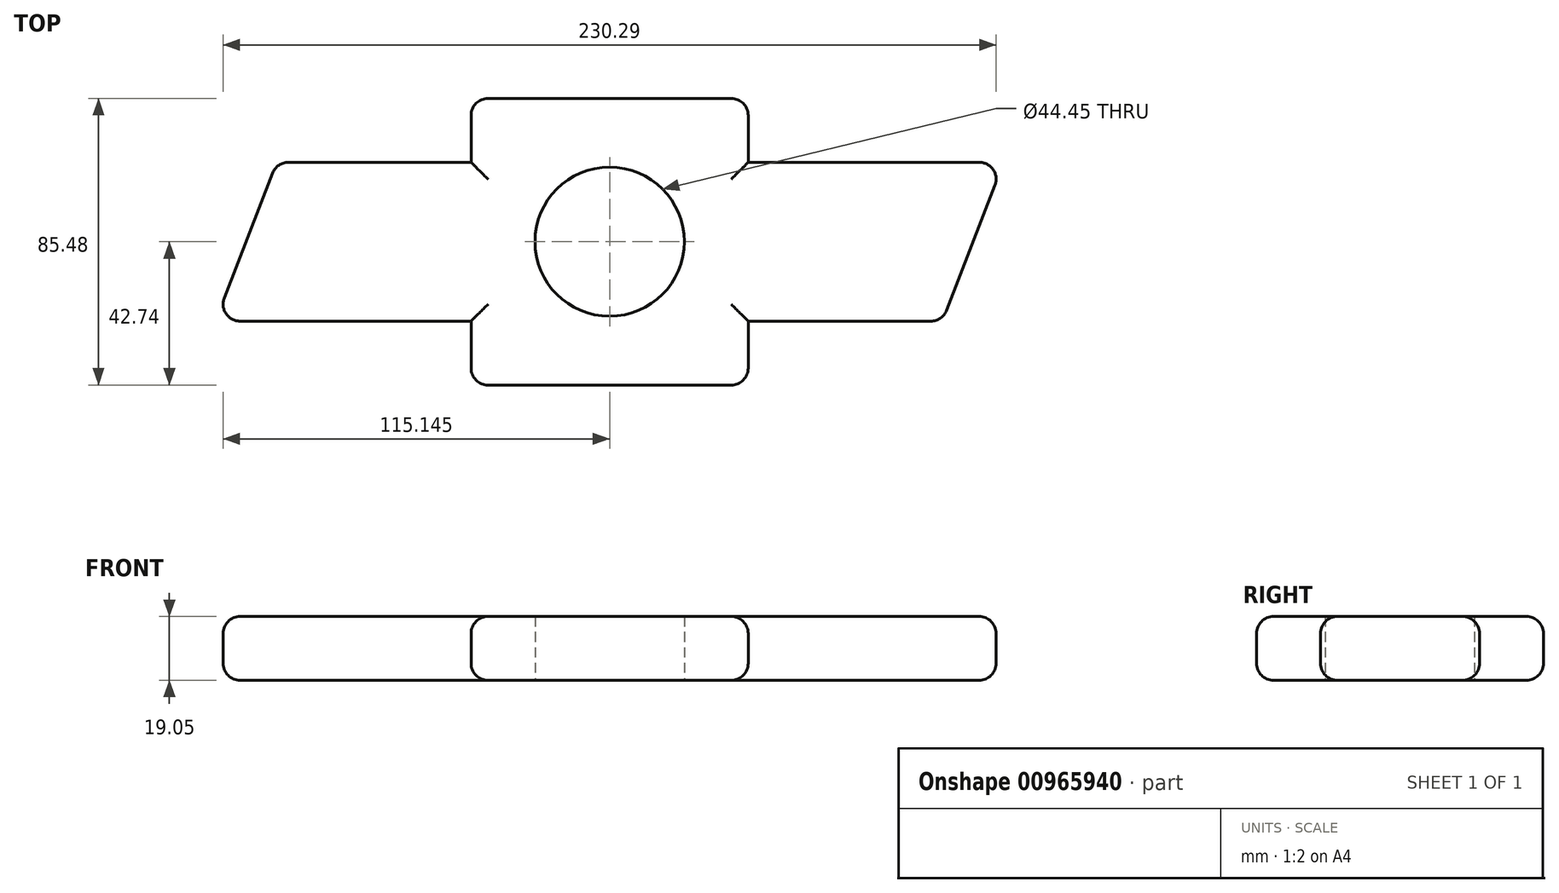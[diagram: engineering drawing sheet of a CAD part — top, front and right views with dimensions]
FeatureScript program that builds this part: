
annotation { "Feature Type Name" : "Feature", "Feature Type Description" : "" }
export const myFeature = defineFeature(function(context is Context, id is Id, definition is map)
    precondition{}
    {
        {
            var Q0;
            Q0=qCreatedBy(makeId("Top.planeOp"),FACE);
            var sketch = newSketch(context, id + "F0", { "sketchPlane" : qUnion([Q0])});
            skLineSegment(sketch, "E0", {"start": v(0, 0) * mm, "end": v(82.55, 0) * mm});
            skLineSegment(sketch, "E1", {"start": v(82.55, 0) * mm, "end": v(82.55, -19.05) * mm});
            skLineSegment(sketch, "E2", {"start": v(82.55, -19.05) * mm, "end": v(158.75, -19.05) * mm});
            skLineSegment(sketch, "E3", {"start": v(158.75, -19.05) * mm, "end": v(140.42, -66.43) * mm});
            skLineSegment(sketch, "E4", {"start": v(0, 0) * mm, "end": v(0, -19.05) * mm});
            skLineSegment(sketch, "E5", {"start": v(0, -19.05) * mm, "end": v(-57.87, -19.05) * mm});
            skLineSegment(sketch, "E6", {"start": v(-57.87, -19.05) * mm, "end": v(-76.2, -66.43) * mm});
            skLineSegment(sketch, "E7", {"start": v(-76.2, -66.43) * mm, "end": v(0, -66.43) * mm});
            skLineSegment(sketch, "E8", {"start": v(0, -66.43) * mm, "end": v(0, -85.48) * mm});
            skLineSegment(sketch, "E9", {"start": v(0, -85.48) * mm, "end": v(82.55, -85.48) * mm});
            skLineSegment(sketch, "E10", {"start": v(82.55, -85.48) * mm, "end": v(82.55, -66.43) * mm});
            skLineSegment(sketch, "E11", {"start": v(82.55, -66.43) * mm, "end": v(140.42, -66.43) * mm});
            skCircle(sketch, "E12", {"center": v(41.28, -42.74) * mm, "radius": 22.23 * mm});
            skSolve(sketch);
        }
        {
            var Q0;
            Q0=makeQuery(id+"F0.imprint","IMPRINT",FACE,{"disambiguationData":[TD([[makeQuery(id+"F0.imprint","IMPRINT",EDGE,{"derivedFrom":sQuery(id+"F0.wireOp",EDGE,"E0")}),-1.0]])]});
            extrude(context, id + "F1", {"entities" : qUnion([Q0]), "depth" : 19.05 * mm, "offsetDistance" : 25.4 * mm});
        }
        {
            var Q0;
            Q0=makeQuery(id+"F1.opExtrude","CAP_EDGE",EDGE,{"disambiguationData":[OSD([sQuery(id+"F0.wireOp",EDGE,"E11")])],"isStart":false});
            var Q1;
            Q1=makeQuery(id+"F1.opExtrude","CAP_EDGE",EDGE,{"disambiguationData":[OSD([sQuery(id+"F0.wireOp",EDGE,"E3")])],"isStart":false});
            var Q2;
            Q2=makeQuery(id+"F1.opExtrude","CAP_EDGE",EDGE,{"disambiguationData":[OSD([sQuery(id+"F0.wireOp",EDGE,"E2")])],"isStart":false});
            var Q3;
            Q3=makeQuery(id+"F1.opExtrude","CAP_EDGE",EDGE,{"disambiguationData":[OSD([sQuery(id+"F0.wireOp",EDGE,"E3")])],"isStart":true});
            var Q4;
            Q4=makeQuery(id+"F1.opExtrude","CAP_EDGE",EDGE,{"disambiguationData":[OSD([sQuery(id+"F0.wireOp",EDGE,"E11")])],"isStart":true});
            var Q5;
            Q5=makeQuery(id+"F1.opExtrude","SWEPT_EDGE",EDGE,{"disambiguationData":[OSD([sQuery(id+"F0.wireOp",EDGE,"E2"),sQuery(id+"F0.wireOp",EDGE,"E3")])]});
            var Q6;
            Q6=makeQuery(id+"F1.opExtrude","SWEPT_EDGE",EDGE,{"disambiguationData":[OSD([sQuery(id+"F0.wireOp",EDGE,"E3"),sQuery(id+"F0.wireOp",EDGE,"E11")])]});
            var Q7;
            Q7=makeQuery(id+"F1.opExtrude","CAP_EDGE",EDGE,{"disambiguationData":[OSD([sQuery(id+"F0.wireOp",EDGE,"E10")])],"isStart":false});
            var Q8;
            Q8=makeQuery(id+"F1.opExtrude","SWEPT_EDGE",EDGE,{"disambiguationData":[OSD([sQuery(id+"F0.wireOp",EDGE,"E9"),sQuery(id+"F0.wireOp",EDGE,"E10")])]});
            var Q9;
            Q9=makeQuery(id+"F1.opExtrude","CAP_EDGE",EDGE,{"disambiguationData":[OSD([sQuery(id+"F0.wireOp",EDGE,"E10")])],"isStart":true});
            var Q10;
            Q10=makeQuery(id+"F1.opExtrude","CAP_EDGE",EDGE,{"disambiguationData":[OSD([sQuery(id+"F0.wireOp",EDGE,"E9")])],"isStart":true});
            var Q11;
            Q11=makeQuery(id+"F1.opExtrude","CAP_EDGE",EDGE,{"disambiguationData":[OSD([sQuery(id+"F0.wireOp",EDGE,"E9")])],"isStart":false});
            var Q12;
            Q12=makeQuery(id+"F1.opExtrude","CAP_EDGE",EDGE,{"disambiguationData":[OSD([sQuery(id+"F0.wireOp",EDGE,"E8")])],"isStart":false});
            var Q13;
            Q13=makeQuery(id+"F1.opExtrude","CAP_EDGE",EDGE,{"disambiguationData":[OSD([sQuery(id+"F0.wireOp",EDGE,"E8")])],"isStart":true});
            var Q14;
            Q14=makeQuery(id+"F1.opExtrude","CAP_EDGE",EDGE,{"disambiguationData":[OSD([sQuery(id+"F0.wireOp",EDGE,"E7")])],"isStart":false});
            var Q15;
            Q15=makeQuery(id+"F1.opExtrude","SWEPT_EDGE",EDGE,{"disambiguationData":[OSD([sQuery(id+"F0.wireOp",EDGE,"E6"),sQuery(id+"F0.wireOp",EDGE,"E7")])]});
            var Q16;
            Q16=makeQuery(id+"F1.opExtrude","CAP_EDGE",EDGE,{"disambiguationData":[OSD([sQuery(id+"F0.wireOp",EDGE,"E7")])],"isStart":true});
            var Q17;
            Q17=makeQuery(id+"F1.opExtrude","CAP_EDGE",EDGE,{"disambiguationData":[OSD([sQuery(id+"F0.wireOp",EDGE,"E6")])],"isStart":false});
            var Q18;
            Q18=makeQuery(id+"F1.opExtrude","CAP_EDGE",EDGE,{"disambiguationData":[OSD([sQuery(id+"F0.wireOp",EDGE,"E6")])],"isStart":true});
            var Q19;
            Q19=makeQuery(id+"F1.opExtrude","SWEPT_EDGE",EDGE,{"disambiguationData":[OSD([sQuery(id+"F0.wireOp",EDGE,"E5"),sQuery(id+"F0.wireOp",EDGE,"E6")])]});
            var Q20;
            Q20=makeQuery(id+"F1.opExtrude","CAP_EDGE",EDGE,{"disambiguationData":[OSD([sQuery(id+"F0.wireOp",EDGE,"E5")])],"isStart":true});
            var Q21;
            Q21=makeQuery(id+"F1.opExtrude","CAP_EDGE",EDGE,{"disambiguationData":[OSD([sQuery(id+"F0.wireOp",EDGE,"E5")])],"isStart":false});
            var Q22;
            Q22=makeQuery(id+"F1.opExtrude","CAP_EDGE",EDGE,{"disambiguationData":[OSD([sQuery(id+"F0.wireOp",EDGE,"E4")])],"isStart":false});
            var Q23;
            Q23=makeQuery(id+"F1.opExtrude","SWEPT_EDGE",EDGE,{"disambiguationData":[OSD([sQuery(id+"F0.wireOp",EDGE,"E0"),sQuery(id+"F0.wireOp",EDGE,"E4")])]});
            var Q24;
            Q24=makeQuery(id+"F1.opExtrude","CAP_EDGE",EDGE,{"disambiguationData":[OSD([sQuery(id+"F0.wireOp",EDGE,"E4")])],"isStart":true});
            var Q25;
            Q25=makeQuery(id+"F1.opExtrude","CAP_EDGE",EDGE,{"disambiguationData":[OSD([sQuery(id+"F0.wireOp",EDGE,"E0")])],"isStart":false});
            var Q26;
            Q26=makeQuery(id+"F1.opExtrude","CAP_EDGE",EDGE,{"disambiguationData":[OSD([sQuery(id+"F0.wireOp",EDGE,"E0")])],"isStart":true});
            var Q27;
            Q27=makeQuery(id+"F1.opExtrude","CAP_EDGE",EDGE,{"disambiguationData":[OSD([sQuery(id+"F0.wireOp",EDGE,"E1")])],"isStart":false});
            var Q28;
            Q28=makeQuery(id+"F1.opExtrude","CAP_EDGE",EDGE,{"disambiguationData":[OSD([sQuery(id+"F0.wireOp",EDGE,"E1")])],"isStart":true});
            var Q29;
            Q29=makeQuery(id+"F1.opExtrude","CAP_EDGE",EDGE,{"disambiguationData":[OSD([sQuery(id+"F0.wireOp",EDGE,"E2")])],"isStart":true});
            var Q30;
            Q30=makeQuery(id+"F1.opExtrude","SWEPT_EDGE",EDGE,{"disambiguationData":[OSD([sQuery(id+"F0.wireOp",EDGE,"E0"),sQuery(id+"F0.wireOp",EDGE,"E1")])]});
            fillet(context, id + "F2", {"entities" : qUnion([Q0, Q1, Q2, Q3, Q4, Q5, Q6, Q7, Q8, Q9, Q10, Q11, Q12, Q13, Q14, Q15, Q16, Q17, Q18, Q19, Q20, Q21, Q22, Q23, Q24, Q25, Q26, Q27, Q28, Q29, Q30]), "radius" : 5.08 * mm, "tangentPropagation" : true, "allowEdgeOverflow" : false});
        }
        {
            var Q0;
            Q0=makeQuery(id+"F1.opExtrude","SWEPT_EDGE",EDGE,{"disambiguationData":[OSD([sQuery(id+"F0.wireOp",EDGE,"E8"),sQuery(id+"F0.wireOp",EDGE,"E9")])]});
            fillet(context, id + "F3", {"entities" : qUnion([Q0]), "radius" : 5.08 * mm, "tangentPropagation" : true, "allowEdgeOverflow" : false});
        }
    });
